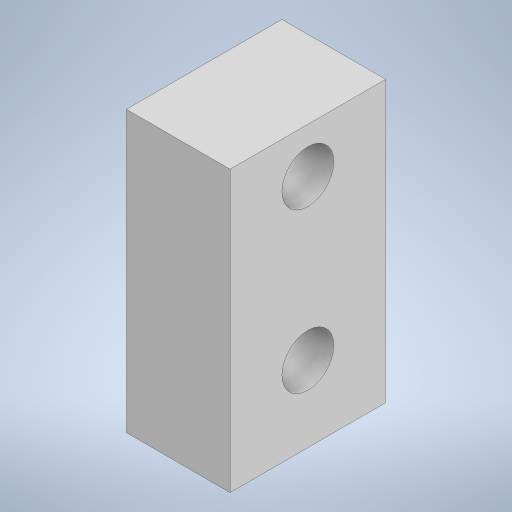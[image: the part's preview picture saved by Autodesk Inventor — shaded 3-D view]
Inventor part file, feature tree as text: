
AUTODESK INVENTOR PART (.ipt)
format: ipt  version: 2024 (Build 280153000, 153)  size: 209,920 bytes
history: native  units: in
note: dims shown in document units (in); Inventor stores cm internally (conversion verified against a paired STEP export)
features: sketch x3, extrude x2
ambient origin geometry x8: Origin, YZ Plane, XZ Plane, XY Plane, X Axis, Y Axis, Z Axis, Center Point
bodies: Solid1 (feature_tree)
feature tree (5):
  extrude  "Extrusion1"  Depth=0.5906in
  extrude  "Extrusion2"  Depth=0.3937in
  sketch  "Sketch3"  dims[d5=0.1969in d6=0.6693in d7=0.1969in d8=0.3937in d9=0.0in]
  sketch  "Sketch1"  dims[d0=1.063in d1=0.5906in]
  sketch  "Sketch2"  dims[d2=0.3937in d3=0.0in d4=0.0709in]
